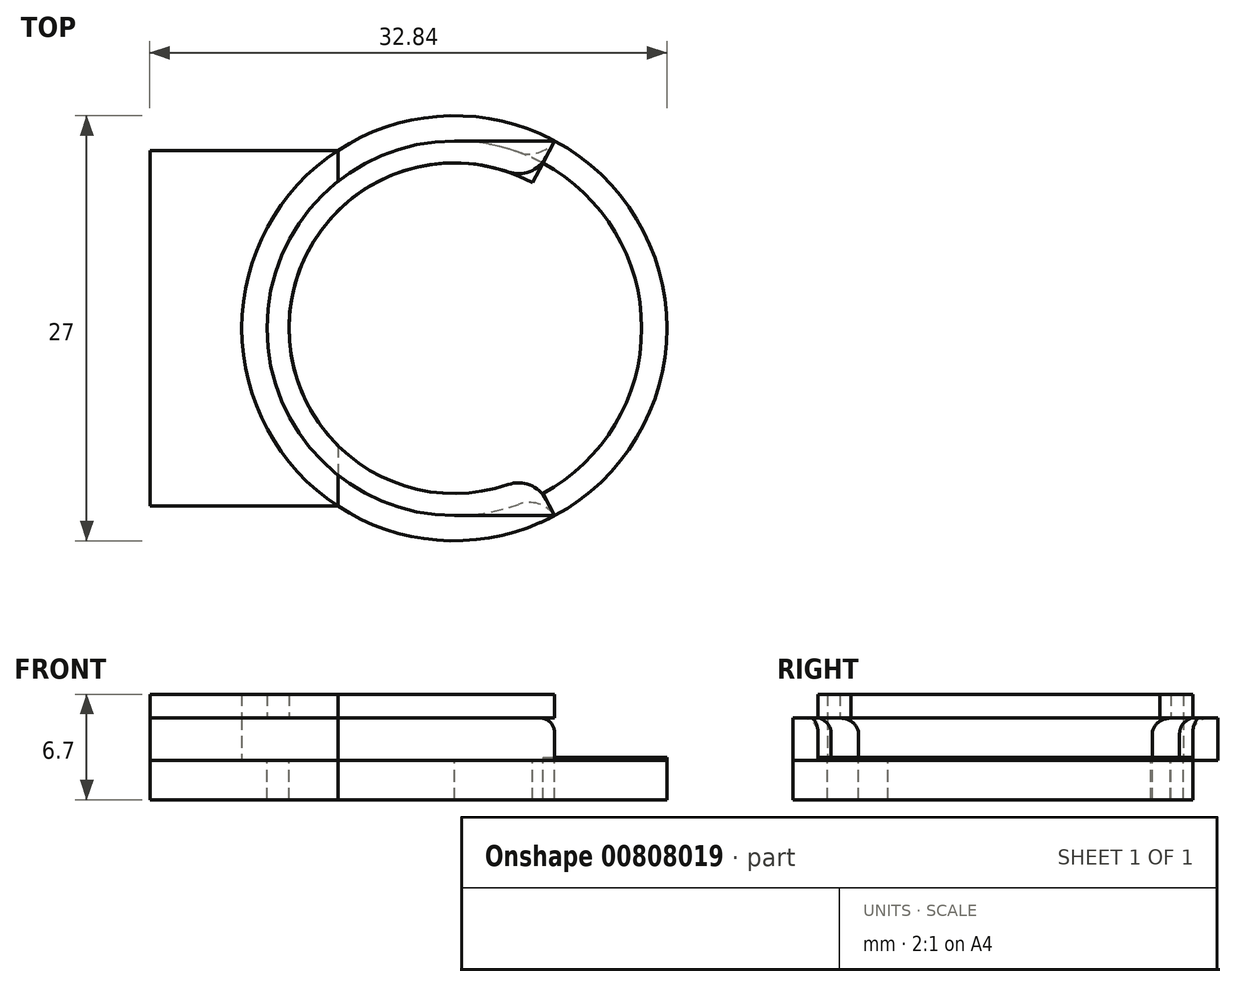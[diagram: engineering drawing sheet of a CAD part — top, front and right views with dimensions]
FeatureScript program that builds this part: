
annotation { "Feature Type Name" : "Feature", "Feature Type Description" : "" }
export const myFeature = defineFeature(function(context is Context, id is Id, definition is map)
    precondition{}
    {
        {
            var Q0;
            Q0=qCreatedBy(makeId("Top.planeOp"),FACE);
            var sketch = newSketch(context, id + "F0", { "sketchPlane" : qUnion([Q0])});
            skCircle(sketch, "E0", {"center": v(0, 0) * mm, "radius": 13.5 * mm});
            skLineSegment(sketch, "E1.bottom", {"start": v(-7.4, 11.3) * mm, "end": v(-19.34, 11.3) * mm});
            skLineSegment(sketch, "E1.top", {"start": v(-7.4, -11.3) * mm, "end": v(-19.34, -11.3) * mm});
            skLineSegment(sketch, "E1.left", {"start": v(-7.4, 11.3) * mm, "end": v(-7.4, -11.3) * mm});
            skLineSegment(sketch, "E1.right", {"start": v(-19.34, 11.3) * mm, "end": v(-19.34, -11.3) * mm});
            skCircle(sketch, "E2.0", {"center": v(0, 0) * mm, "radius": 10.5 * mm});
            skCircle(sketch, "E3", {"center": v(0, 0) * mm, "radius": 11.9 * mm});
            skLineSegment(sketch, "E4", {"start": v(-19.34, -11.3) * mm, "end": v(52.97, -11.3) * mm, "construction": true});
            skLineSegment(sketch, "E5", {"start": v(0, 11.9) * mm, "end": v(6.37, 11.9) * mm});
            skLineSegment(sketch, "E6", {"start": v(0, -11.9) * mm, "end": v(6.37, -11.9) * mm});
            skLineSegment(sketch, "E7", {"start": v(4.96, 9.26) * mm, "end": v(6.37, 11.9) * mm});
            skLineSegment(sketch, "E8", {"start": v(4.96, -9.26) * mm, "end": v(6.37, -11.9) * mm});
            skSolve(sketch);
        }
        {
            var Q0;
            {var subQ1=sQuery(id+"F0.wireOp",EDGE,"E1.bottom");Q0=makeQuery(id+"F0.imprint","IMPRINT",FACE,{"disambiguationData":[TD([[makeQuery(id+"F0.imprint","IMPRINT",EDGE,{"derivedFrom":subQ1}),1.0]])]});}
            var Q1;
            {var subQ0=sQuery(id+"F0.wireOp",EDGE,"E2.0");var subQ1=sQuery(id+"F0.wireOp",EDGE,"E1.left");var subQ2=makeQuery(id+"F0.imprint","INTERSECT",VERTEX,{"disambiguationData":[OD(0.0)],"derivedFrom":[subQ1,subQ0]});Q1=makeQuery(id+"F0.imprint","IMPRINT",FACE,{"disambiguationData":[TD([[makeQuery(id+"F0.imprint","IMPRINT",EDGE,{"disambiguationData":[TD([[subQ2,-1.0]])],"derivedFrom":subQ1}),1.0]])]});}
            var Q2;
            {var subQ0=sQuery(id+"F0.wireOp",EDGE,"E3");var subQ1=sQuery(id+"F0.wireOp",EDGE,"E1.left");var subQ2=makeQuery(id+"F0.imprint","INTERSECT",VERTEX,{"disambiguationData":[OD(0.0)],"derivedFrom":[subQ1,subQ0]});Q2=makeQuery(id+"F0.imprint","IMPRINT",FACE,{"disambiguationData":[TD([[makeQuery(id+"F0.imprint","IMPRINT",EDGE,{"disambiguationData":[TD([[subQ2,-1.0]])],"derivedFrom":subQ1}),1.0]])]});}
            var Q3;
            {var subQ0=sQuery(id+"F0.wireOp",EDGE,"E1.left");var subQ4=sQuery(id+"F0.wireOp",EDGE,"E3");var subQ5=makeQuery(id+"F0.imprint","INTERSECT",VERTEX,{"disambiguationData":[OD(0.0)],"derivedFrom":[subQ0,subQ4]});Q3=makeQuery(id+"F0.imprint","IMPRINT",FACE,{"disambiguationData":[TD([[makeQuery(id+"F0.imprint","IMPRINT",EDGE,{"disambiguationData":[TD([[subQ5,1.0]])],"derivedFrom":subQ4}),-1.0]])]});}
            var Q4;
            {var subQ0=sQuery(id+"F0.wireOp",EDGE,"E2.0");var subQ1=sQuery(id+"F0.wireOp",EDGE,"E1.left");var subQ2=makeQuery(id+"F0.imprint","INTERSECT",VERTEX,{"disambiguationData":[OD(0.0)],"derivedFrom":[subQ1,subQ0]});Q4=makeQuery(id+"F0.imprint","IMPRINT",FACE,{"disambiguationData":[TD([[makeQuery(id+"F0.imprint","IMPRINT",EDGE,{"disambiguationData":[TD([[subQ2,-1.0]])],"derivedFrom":subQ1}),-1.0]])]});}
            var Q5;
            {var subQ0=sQuery(id+"F0.wireOp",EDGE,"E3");var subQ1=sQuery(id+"F0.wireOp",EDGE,"E1.left");var subQ2=makeQuery(id+"F0.imprint","INTERSECT",VERTEX,{"disambiguationData":[OD(0.0)],"derivedFrom":[subQ1,subQ0]});Q5=makeQuery(id+"F0.imprint","IMPRINT",FACE,{"disambiguationData":[TD([[makeQuery(id+"F0.imprint","IMPRINT",EDGE,{"disambiguationData":[TD([[subQ2,-1.0]])],"derivedFrom":subQ1}),-1.0]])]});}
            var Q6;
            {var subQ0=sQuery(id+"F0.wireOp",EDGE,"E1.left");var subQ4=sQuery(id+"F0.wireOp",EDGE,"E3");var subQ5=makeQuery(id+"F0.imprint","INTERSECT",VERTEX,{"disambiguationData":[OD(0.0)],"derivedFrom":[subQ0,subQ4]});Q6=makeQuery(id+"F0.imprint","IMPRINT",FACE,{"disambiguationData":[TD([[makeQuery(id+"F0.imprint","IMPRINT",EDGE,{"disambiguationData":[TD([[subQ5,-1.0]])],"derivedFrom":subQ4}),-1.0]])]});}
            var Q7;
            {var subQ0=sQuery(id+"F0.wireOp",EDGE,"E5");Q7=makeQuery(id+"F0.imprint","IMPRINT",FACE,{"disambiguationData":[TD([[makeQuery(id+"F0.imprint","IMPRINT",EDGE,{"derivedFrom":subQ0}),-1.0]])]});}
            var Q8;
            {var subQ3=sQuery(id+"F0.wireOp",EDGE,"E6");Q8=makeQuery(id+"F0.imprint","IMPRINT",FACE,{"disambiguationData":[TD([[makeQuery(id+"F0.imprint","IMPRINT",EDGE,{"derivedFrom":subQ3}),-1.0]])]});}
            var Q9;
            {var subQ0=sQuery(id+"F0.wireOp",EDGE,"E7");var subQ1=sQuery(id+"F0.wireOp",EDGE,"E2.0");var subQ2=makeQuery(id+"F0.imprint","INTERSECT",VERTEX,{"derivedFrom":[subQ1,subQ0]});Q9=makeQuery(id+"F0.imprint","IMPRINT",FACE,{"disambiguationData":[TD([[makeQuery(id+"F0.imprint","IMPRINT",EDGE,{"disambiguationData":[TD([[subQ2,1.0]])],"derivedFrom":subQ1}),-1.0]])]});}
            var Q10;
            {var subQ0=sQuery(id+"F0.wireOp",EDGE,"E7");var subQ5=sQuery(id+"F0.wireOp",EDGE,"E3");var subQ6=makeQuery(id+"F0.imprint","INTERSECT",VERTEX,{"derivedFrom":[subQ5,subQ0]});Q10=makeQuery(id+"F0.imprint","IMPRINT",FACE,{"disambiguationData":[TD([[makeQuery(id+"F0.imprint","IMPRINT",EDGE,{"disambiguationData":[TD([[subQ6,1.0]])],"derivedFrom":subQ5}),-1.0]])]});}
            var Q11;
            {var subQ4=sQuery(id+"F0.wireOp",EDGE,"E2.0");var subQ5=sQuery(id+"F0.wireOp",EDGE,"E1.left");var subQ6=makeQuery(id+"F0.imprint","INTERSECT",VERTEX,{"disambiguationData":[OD(1.0)],"derivedFrom":[subQ5,subQ4]});Q11=makeQuery(id+"F0.imprint","IMPRINT",FACE,{"disambiguationData":[TD([[makeQuery(id+"F0.imprint","IMPRINT",EDGE,{"disambiguationData":[TD([[subQ6,-1.0]])],"derivedFrom":subQ5}),1.0]])]});}
            var Q12;
            {var subQ0=sQuery(id+"F0.wireOp",EDGE,"E6");Q12=makeQuery(id+"F0.imprint","IMPRINT",FACE,{"disambiguationData":[TD([[makeQuery(id+"F0.imprint","IMPRINT",EDGE,{"derivedFrom":subQ0}),1.0]])]});}
            extrude(context, id + "F1", {"entities" : qUnion([Q0, Q1, Q2, Q3, Q4, Q5, Q6, Q7, Q8, Q9, Q10, Q11, Q12]), "oppositeDirection" : true, "depth" : 2.5 * mm, "offsetDistance" : 25 * mm});
        }
        {
            var Q0;
            {var subQ1=sQuery(id+"F0.wireOp",EDGE,"E1.bottom");Q0=makeQuery(id+"F0.imprint","IMPRINT",FACE,{"disambiguationData":[TD([[makeQuery(id+"F0.imprint","IMPRINT",EDGE,{"derivedFrom":subQ1}),1.0]])]});}
            var Q1;
            {var subQ3=sQuery(id+"F0.wireOp",EDGE,"E5");Q1=makeQuery(id+"F0.imprint","IMPRINT",FACE,{"disambiguationData":[TD([[makeQuery(id+"F0.imprint","IMPRINT",EDGE,{"derivedFrom":subQ3}),1.0]])]});}
            var Q2;
            {var subQ3=sQuery(id+"F0.wireOp",EDGE,"E6");Q2=makeQuery(id+"F0.imprint","IMPRINT",FACE,{"disambiguationData":[TD([[makeQuery(id+"F0.imprint","IMPRINT",EDGE,{"derivedFrom":subQ3}),-1.0]])]});}
            var Q3;
            {var subQ0=sQuery(id+"F0.wireOp",EDGE,"E1.left");var subQ4=sQuery(id+"F0.wireOp",EDGE,"E3");var subQ5=makeQuery(id+"F0.imprint","INTERSECT",VERTEX,{"disambiguationData":[OD(0.0)],"derivedFrom":[subQ0,subQ4]});Q3=makeQuery(id+"F0.imprint","IMPRINT",FACE,{"disambiguationData":[TD([[makeQuery(id+"F0.imprint","IMPRINT",EDGE,{"disambiguationData":[TD([[subQ5,-1.0]])],"derivedFrom":subQ4}),-1.0]])]});}
            var Q4;
            {var subQ0=sQuery(id+"F0.wireOp",EDGE,"E5");Q4=makeQuery(id+"F0.imprint","IMPRINT",FACE,{"disambiguationData":[TD([[makeQuery(id+"F0.imprint","IMPRINT",EDGE,{"derivedFrom":subQ0}),-1.0]])]});}
            var Q5;
            {var subQ0=sQuery(id+"F0.wireOp",EDGE,"E6");Q5=makeQuery(id+"F0.imprint","IMPRINT",FACE,{"disambiguationData":[TD([[makeQuery(id+"F0.imprint","IMPRINT",EDGE,{"derivedFrom":subQ0}),1.0]])]});}
            extrude(context, id + "F2", {"entities" : qUnion([Q0, Q1, Q2, Q3, Q4, Q5]), "depth" : 2.7 * mm, "offsetDistance" : 25 * mm});
        }
        {
            var Q0;
            Q0=makeQuery(id+"F2.opExtrude","CAP_FACE",FACE,{"disambiguationData":[OSD([sQuery(id+"F0.wireOp",EDGE,"E0"),sQuery(id+"F0.wireOp",EDGE,"E1.bottom"),sQuery(id+"F0.wireOp",EDGE,"E1.top"),sQuery(id+"F0.wireOp",EDGE,"E1.right"),sQuery(id+"F0.wireOp",EDGE,"E3"),sQuery(id+"F0.wireOp",EDGE,"E5"),sQuery(id+"F0.wireOp",EDGE,"E6")])],"isStart":false});
            var sketch = newSketch(context, id + "F3", { "sketchPlane" : qUnion([Q0])});
            skLineSegment(sketch, "E9.0.0", {"start": v(-19.34, -11.3) * mm, "end": v(-7.4, -11.3) * mm});
            skArc(sketch, "E9.0.1", {"start": v(-7.4, -11.3) * mm, "mid": v(-0.6, -13.49) * mm, "end": v(6.37, -11.9) * mm});
            skLineSegment(sketch, "E9.0.2", {"start": v(6.37, -11.9) * mm, "end": v(0, -11.9) * mm});
            skArc(sketch, "E9.0.3", {"start": v(0, -11.9) * mm, "mid": v(-11.54, 2.9) * mm, "end": v(5.62, 10.49) * mm});
            skLineSegment(sketch, "E9.0.4", {"start": v(5.62, 10.49) * mm, "end": v(6.37, 11.9) * mm});
            skArc(sketch, "E9.0.5", {"start": v(6.37, 11.9) * mm, "mid": v(-0.6, 13.49) * mm, "end": v(-7.4, 11.3) * mm});
            skLineSegment(sketch, "E9.0.6", {"start": v(-7.4, 11.3) * mm, "end": v(-19.34, 11.3) * mm});
            skLineSegment(sketch, "E9.0.7", {"start": v(-19.34, 11.3) * mm, "end": v(-19.34, -11.3) * mm});
            skCircle(sketch, "E10.0", {"center": v(0, 0) * mm, "radius": 10.5 * mm});
            skLineSegment(sketch, "E11.0", {"start": v(0, -11.9) * mm, "end": v(6.37, -11.9) * mm});
            skLineSegment(sketch, "E12.0", {"start": v(4.96, -9.26) * mm, "end": v(6.37, -11.9) * mm});
            skLineSegment(sketch, "E13.0", {"start": v(4.96, 9.26) * mm, "end": v(6.37, 11.9) * mm});
            skLineSegment(sketch, "E14.0", {"start": v(0, 11.9) * mm, "end": v(6.37, 11.9) * mm});
            skSolve(sketch);
        }
        {
            var Q0;
            Q0=makeQuery(id+"F3.imprint","IMPRINT",FACE,{"disambiguationData":[TD([[makeQuery(id+"F3.imprint","IMPRINT",EDGE,{"derivedFrom":sQuery(id+"F3.wireOp",EDGE,"E9.0.0")}),-1.0]])]});
            var Q1;
            Q1=makeQuery(id+"F3.imprint","IMPRINT",FACE,{"disambiguationData":[TD([[makeQuery(id+"F3.imprint","IMPRINT",EDGE,{"derivedFrom":sQuery(id+"F3.wireOp",EDGE,"E9.0.3")}),1.0]])]});
            var Q2;
            {var subQ0=sQuery(id+"F3.wireOp",EDGE,"E11.0");Q2=makeQuery(id+"F3.imprint","IMPRINT",FACE,{"disambiguationData":[TD([[makeQuery(id+"F3.imprint","IMPRINT",EDGE,{"derivedFrom":subQ0}),1.0]])]});}
            var Q3;
            {var subQ3=sQuery(id+"F3.wireOp",EDGE,"E14.0");Q3=makeQuery(id+"F3.imprint","IMPRINT",FACE,{"disambiguationData":[TD([[makeQuery(id+"F3.imprint","IMPRINT",EDGE,{"derivedFrom":subQ3}),-1.0]])]});}
            extrude(context, id + "F4", {"entities" : qUnion([Q0, Q1, Q2, Q3]), "depth" : 1.5 * mm, "offsetDistance" : 25 * mm});
        }
        {
            var Q0;
            {var subQ0=sQuery(id+"F0.wireOp",EDGE,"E7");var subQ5=sQuery(id+"F0.wireOp",EDGE,"E3");var subQ6=makeQuery(id+"F0.imprint","INTERSECT",VERTEX,{"derivedFrom":[subQ5,subQ0]});Q0=makeQuery(id+"F0.imprint","IMPRINT",FACE,{"disambiguationData":[TD([[makeQuery(id+"F0.imprint","IMPRINT",EDGE,{"disambiguationData":[TD([[subQ6,1.0]])],"derivedFrom":subQ5}),-1.0]])]});}
            extrude(context, id + "F5", {"entities" : qUnion([Q0]), "depth" : 0.2 * mm, "offsetDistance" : 25 * mm});
        }
        {
            var Q0;
            Q0=makeQuery(id+"F4.opExtrude","SWEPT_EDGE",EDGE,{"disambiguationData":[OSD([sQuery(id+"F3.wireOp",EDGE,"E10.0"),sQuery(id+"F3.wireOp",EDGE,"E12.0")])]});
            var Q1;
            Q1=makeQuery(id+"F4.opExtrude","SWEPT_EDGE",EDGE,{"disambiguationData":[OSD([sQuery(id+"F3.wireOp",EDGE,"E10.0"),sQuery(id+"F3.wireOp",EDGE,"E13.0")])]});
            var Q2;
            Q2=makeQuery(id+"F2.opExtrude","SWEPT_EDGE",EDGE,{"disambiguationData":[OSD([sQuery(id+"F0.wireOp",EDGE,"E3"),sQuery(id+"F0.wireOp",EDGE,"E7")])]});
            var Q3;
            Q3=makeQuery(id+"F2.opExtrude","SWEPT_EDGE",EDGE,{"disambiguationData":[OSD([sQuery(id+"F0.wireOp",EDGE,"E3"),sQuery(id+"F0.wireOp",EDGE,"E8")])]});
            fillet(context, id + "F6", {"entities" : qUnion([Q0, Q1, Q2, Q3]), "radius" : 2 * mm, "tangentPropagation" : true, "allowEdgeOverflow" : false});
        }
        {
            var Q0;
            Q0=makeQuery(id+"F2.opExtrude","CAP_EDGE",EDGE,{"disambiguationData":[OSD([sQuery(id+"F0.wireOp",EDGE,"E3")])],"isStart":false});
            fillet(context, id + "F7", {"entities" : qUnion([Q0]), "radius" : 1 * mm, "tangentPropagation" : true, "allowEdgeOverflow" : false});
        }
    });
